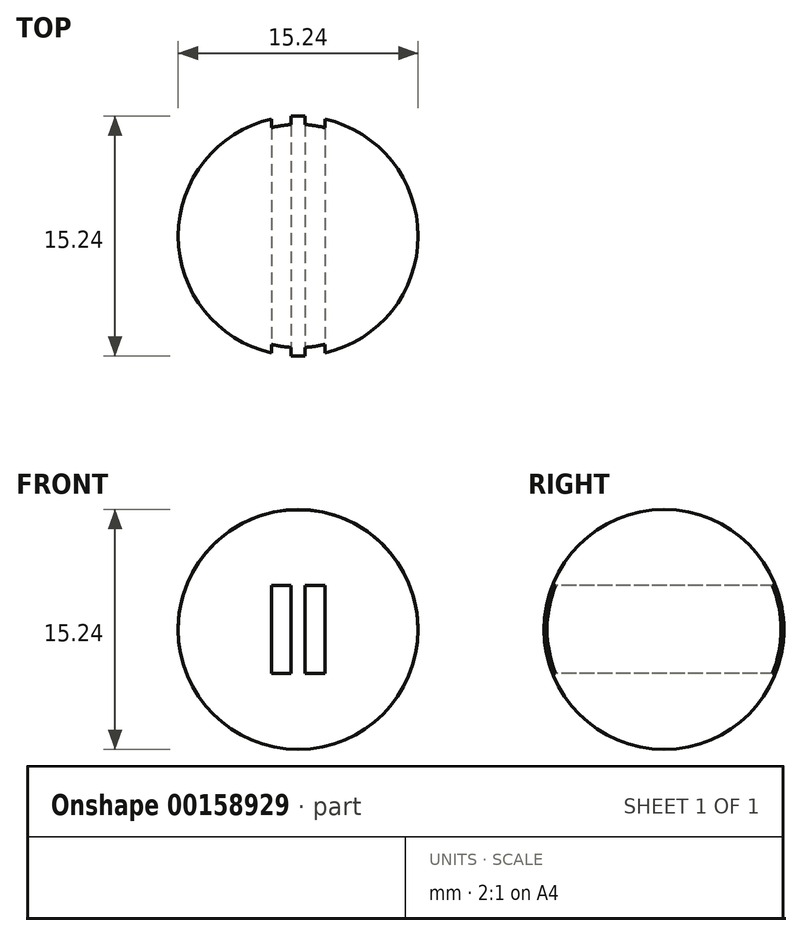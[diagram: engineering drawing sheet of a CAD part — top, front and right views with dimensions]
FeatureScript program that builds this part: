
annotation { "Feature Type Name" : "Feature", "Feature Type Description" : "" }
export const myFeature = defineFeature(function(context is Context, id is Id, definition is map)
    precondition{}
    {
        {
            var Q0;
            Q0=qCreatedBy(makeId("Front.planeOp"),FACE);
            var sketch = newSketch(context, id + "F0", { "sketchPlane" : qUnion([Q0])});
            skArc(sketch, "E0", {"start": v(7.62, 0) * mm, "mid": v(0, 7.62) * mm, "end": v(-7.62, 0) * mm});
            skLineSegment(sketch, "E1", {"start": v(-7.62, 0) * mm, "end": v(7.62, 0) * mm});
            skSolve(sketch);
        }
        {
            var Q0;
            Q0=makeQuery(id+"F0.imprint","IMPRINT",FACE,{"disambiguationData":[TD([[makeQuery(id+"F0.imprint","IMPRINT",EDGE,{"derivedFrom":sQuery(id+"F0.wireOp",EDGE,"E0")}),1.0]])]});
            var Q1;
            Q1=sQuery(id+"F0.wireOp",EDGE,"E1");
            revolve(context, id + "F1", {"entities" : qUnion([Q0]), "axis" : qUnion([Q1]), "revolveType" : RevolveType.FULL});
        }
        {
            var Q0;
            Q0=qCreatedBy(makeId("Front.planeOp"),FACE);
            cPlane(context, id + "F2", {"entities" : qUnion([Q0]), "cplaneType" : CPlaneType.OFFSET, "offset" : 8.9 * mm, "width" : 152.4 * mm, "height" : 152.4 * mm});
        }
        {
            var Q0;
            Q0=qCreatedBy(id+"F2.planeOp",FACE);
            var sketch = newSketch(context, id + "F3", { "sketchPlane" : qUnion([Q0])});
            skLineSegment(sketch, "E2.bottom", {"start": v(-0.45, 2.8) * mm, "end": v(-1.7, 2.8) * mm});
            skLineSegment(sketch, "E2.top", {"start": v(-0.45, -2.8) * mm, "end": v(-1.7, -2.8) * mm});
            skLineSegment(sketch, "E2.left", {"start": v(-0.45, 2.8) * mm, "end": v(-0.45, -2.8) * mm});
            skLineSegment(sketch, "E2.right", {"start": v(-1.7, 2.8) * mm, "end": v(-1.7, -2.8) * mm});
            skPoint(sketch, "E2.middle", {"position": v(-1.07, 0) * mm});
            skLineSegment(sketch, "E3.MirrorCS", {"start": v(0.45, 2.8) * mm, "end": v(1.7, 2.8) * mm});
            skLineSegment(sketch, "E4.MirrorCS", {"start": v(1.7, 2.8) * mm, "end": v(1.7, -2.8) * mm});
            skLineSegment(sketch, "E5.MirrorCS", {"start": v(0.45, 2.8) * mm, "end": v(0.45, -2.8) * mm});
            skLineSegment(sketch, "E6.MirrorCS", {"start": v(0.45, -2.8) * mm, "end": v(1.7, -2.8) * mm});
            skSolve(sketch);
        }
        {
            var Q0;
            Q0 = qSketchRegion(id + "F3", true);
            extrude(context, id + "F4", {"entities" : qUnion([Q0]), "operationType" : NewBodyOperationType.REMOVE, "oppositeDirection" : true, "depth" : 25.4 * mm});
        }
    });
